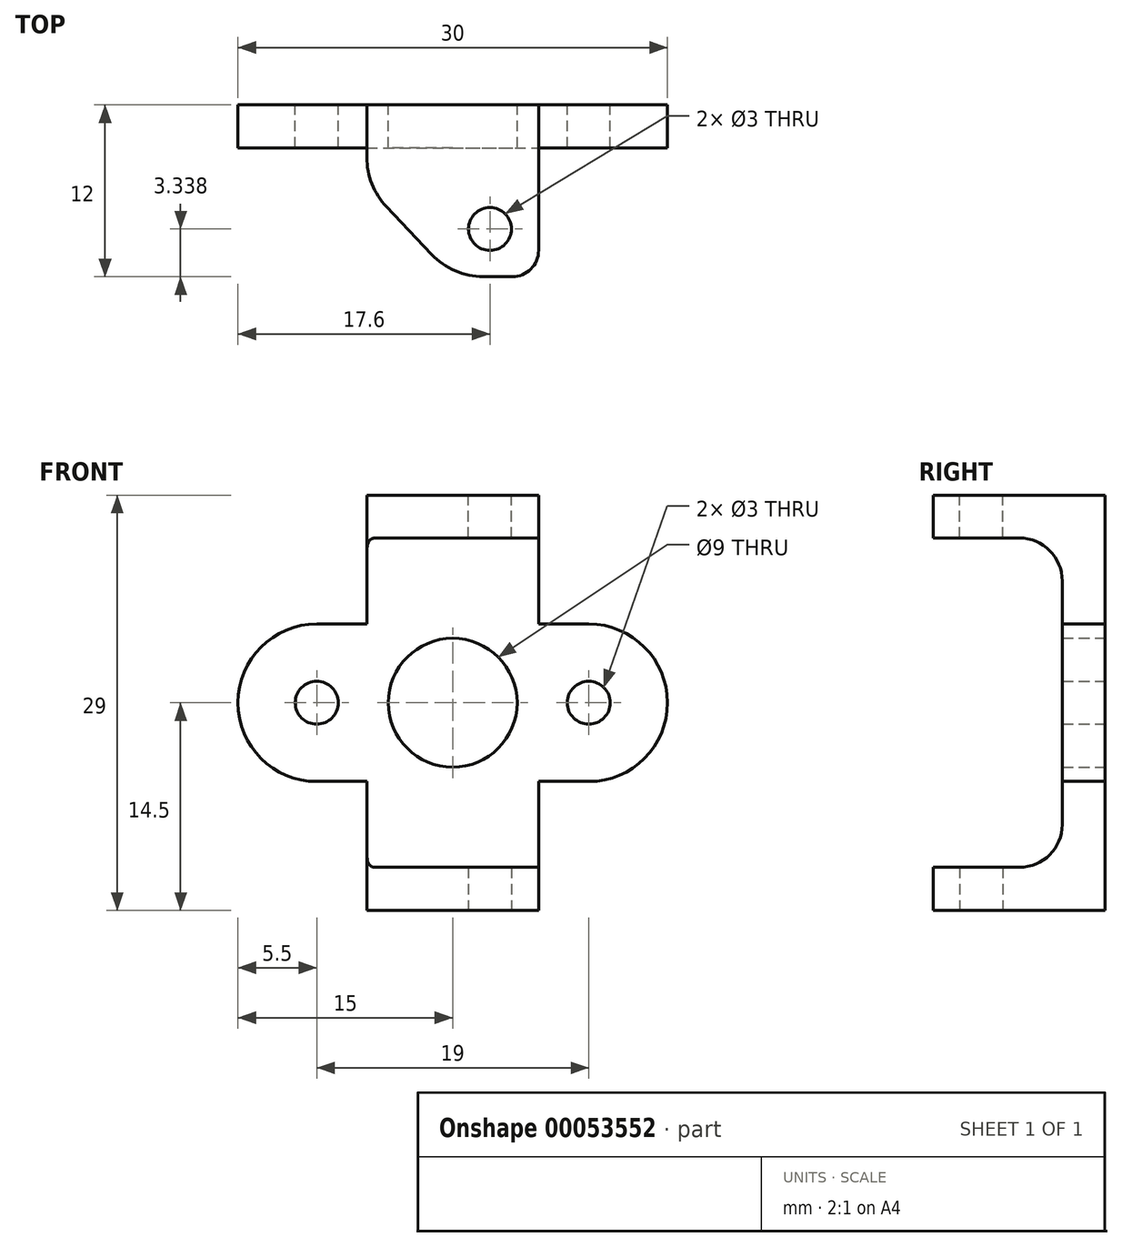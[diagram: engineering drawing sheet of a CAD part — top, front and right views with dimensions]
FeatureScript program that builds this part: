
annotation { "Feature Type Name" : "Feature", "Feature Type Description" : "" }
export const myFeature = defineFeature(function(context is Context, id is Id, definition is map)
    precondition{}
    {
        {
            var Q0;
            Q0=qCreatedBy(makeId("Front.planeOp"),FACE);
            var sketch = newSketch(context, id + "F0", { "sketchPlane" : qUnion([Q0])});
            skCircle(sketch, "E0", {"center": v(0, 0) * mm, "radius": 4.5 * mm});
            skCircle(sketch, "E1", {"center": v(9.5, 0) * mm, "radius": 1.5 * mm});
            skCircle(sketch, "E2.MirrorC", {"center": v(-9.5, 0) * mm, "radius": 1.5 * mm});
            skArc(sketch, "E3.0", {"start": v(9.5, -5.5) * mm, "mid": v(15, 0) * mm, "end": v(9.5, 5.5) * mm});
            skLineSegment(sketch, "E4", {"start": v(9.5, 7.45) * mm, "end": v(9.5, -7.59) * mm, "construction": true});
            skLineSegment(sketch, "E5", {"start": v(9.5, -5.5) * mm, "end": v(0, -5.5) * mm});
            skLineSegment(sketch, "E6.MirrorCS", {"start": v(9.5, 5.5) * mm, "end": v(0, 5.5) * mm});
            skArc(sketch, "E7.MirrorCS", {"start": v(-9.5, -5.5) * mm, "mid": v(-15, 0) * mm, "end": v(-9.5, 5.5) * mm});
            skLineSegment(sketch, "E8.MirrorCS", {"start": v(-9.5, 5.5) * mm, "end": v(0, 5.5) * mm});
            skLineSegment(sketch, "E9.MirrorCS", {"start": v(-9.5, -5.5) * mm, "end": v(0, -5.5) * mm});
            skSolve(sketch);
        }
        {
            var Q0;
            Q0 = qSketchRegion(id + "F0", true);
            extrude(context, id + "F1", {"entities" : qUnion([Q0]), "depth" : 3 * mm});
        }
        {
            var Q0;
            Q0=makeQuery(id+"F1.opExtrude","CAP_FACE",FACE,{"disambiguationData":[OSD([sQuery(id+"F0.wireOp",EDGE,"E0"),sQuery(id+"F0.wireOp",EDGE,"E1"),sQuery(id+"F0.wireOp",EDGE,"E2.MirrorC"),sQuery(id+"F0.wireOp",EDGE,"E3.0"),sQuery(id+"F0.wireOp",EDGE,"E5"),sQuery(id+"F0.wireOp",EDGE,"E6.MirrorCS"),sQuery(id+"F0.wireOp",EDGE,"E7.MirrorCS"),sQuery(id+"F0.wireOp",EDGE,"E8.MirrorCS"),sQuery(id+"F0.wireOp",EDGE,"E9.MirrorCS")])],"isStart":false});
            var sketch = newSketch(context, id + "F2", { "sketchPlane" : qUnion([Q0])});
            skLineSegment(sketch, "E10.rect.bottom", {"start": v(6, -14.5) * mm, "end": v(-6, -14.5) * mm});
            skLineSegment(sketch, "E10.rect.top", {"start": v(6, 14.5) * mm, "end": v(-6, 14.5) * mm});
            skLineSegment(sketch, "E10.rect.left", {"start": v(6, -14.5) * mm, "end": v(6, 14.5) * mm});
            skLineSegment(sketch, "E10.rect.right", {"start": v(-6, -14.5) * mm, "end": v(-6, 14.5) * mm});
            skPoint(sketch, "E10.rect.middle", {"position": v(0, 0) * mm});
            skSolve(sketch);
        }
        {
            var Q0;
            Q0 = qSketchRegion(id + "F2", true);
            extrude(context, id + "F3", {"entities" : qUnion([Q0]), "operationType" : NewBodyOperationType.ADD, "oppositeDirection" : true, "depth" : 3 * mm});
        }
        {
            var Q0;
            Q0=makeQuery(id+"F3.opExtrude","SWEPT_FACE",FACE,{"disambiguationData":[OSD([sQuery(id+"F2.wireOp",EDGE,"E10.rect.bottom")])]});
            var sketch = newSketch(context, id + "F4", { "sketchPlane" : qUnion([Q0])});
            skLineSegment(sketch, "E11.bottom", {"start": v(6, 0) * mm, "end": v(-6, 0) * mm});
            skLineSegment(sketch, "E11.top", {"start": v(4.15, 12) * mm, "end": v(2.15, 12) * mm});
            skLineSegment(sketch, "E11.left", {"start": v(6, 0) * mm, "end": v(6, 10.15) * mm});
            skLineSegment(sketch, "E11.right", {"start": v(-6, 0) * mm, "end": v(-6, 3.67) * mm});
            skPoint(sketch, "E12.visualSharp", {"position": v(6, 12) * mm});
            skArc(sketch, "E12.filletArc", {"start": v(6, 10.15) * mm, "mid": v(5.46, 11.46) * mm, "end": v(4.15, 12) * mm});
            skCircle(sketch, "E13", {"center": v(2.6, 8.66) * mm, "radius": 1.5 * mm});
            skLineSegment(sketch, "E14", {"start": v(-1.48, 10.44) * mm, "end": v(-4.63, 7.11) * mm});
            skPoint(sketch, "E15.orphan", {"position": v(-6, 12) * mm});
            skPoint(sketch, "E16.visualSharp", {"position": v(-6, 5.67) * mm});
            skArc(sketch, "E16.filletArc", {"start": v(-4.63, 7.11) * mm, "mid": v(-5.64, 5.53) * mm, "end": v(-6, 3.67) * mm});
            skPoint(sketch, "E17.visualSharp", {"position": v(0, 12) * mm});
            skArc(sketch, "E17.filletArc", {"start": v(2.15, 12) * mm, "mid": v(0.17, 11.6) * mm, "end": v(-1.48, 10.44) * mm});
            skSolve(sketch);
        }
        {
            var Q0;
            Q0 = qSketchRegion(id + "F4", true);
            extrude(context, id + "F5", {"entities" : qUnion([Q0]), "oppositeDirection" : true, "depth" : 3 * mm});
        }
        {
            var Q0;
            Q0=makeQuery(id+"F5.opExtrude","SWEPT_BODY",BODY,{"disambiguationData":[OSD([sQuery(id+"F4.wireOp",EDGE,"E11.bottom"),sQuery(id+"F4.wireOp",EDGE,"E11.top"),sQuery(id+"F4.wireOp",EDGE,"E11.left"),sQuery(id+"F4.wireOp",EDGE,"E11.right"),sQuery(id+"F4.wireOp",EDGE,"E12.filletArc"),sQuery(id+"F4.wireOp",EDGE,"E13"),sQuery(id+"F4.wireOp",EDGE,"E14"),sQuery(id+"F4.wireOp",EDGE,"E16.filletArc"),sQuery(id+"F4.wireOp",EDGE,"E17.filletArc")])]});
            var Q1;
            Q1=qCreatedBy(makeId("Top.planeOp"),FACE);
            mirror(context, id + "F6", {"operationType" : NewBodyOperationType.ADD, "entities" : qUnion([Q0]), "mirrorPlane" : qUnion([Q1])});
        }
        {
            var Q0;
            Q0=makeQuery(id+"F6.boolean.opBoolean","INTERSECT",EDGE,{"derivedFrom":[makeQuery(id+"F3.boolean.opBoolean","MERGE",FACE,{"derivedFrom":[makeQuery(id+"F1.opExtrude","CAP_FACE",FACE,{"disambiguationData":[OSD([sQuery(id+"F0.wireOp",EDGE,"E0"),sQuery(id+"F0.wireOp",EDGE,"E1"),sQuery(id+"F0.wireOp",EDGE,"E2.MirrorC"),sQuery(id+"F0.wireOp",EDGE,"E3.0"),sQuery(id+"F0.wireOp",EDGE,"E5"),sQuery(id+"F0.wireOp",EDGE,"E6.MirrorCS"),sQuery(id+"F0.wireOp",EDGE,"E7.MirrorCS"),sQuery(id+"F0.wireOp",EDGE,"E8.MirrorCS"),sQuery(id+"F0.wireOp",EDGE,"E9.MirrorCS")])],"isStart":false}),makeQuery(id+"F3.opExtrude","CAP_FACE",FACE,{"disambiguationData":[OSD([sQuery(id+"F2.wireOp",EDGE,"E10.rect.bottom"),sQuery(id+"F2.wireOp",EDGE,"E10.rect.top"),sQuery(id+"F2.wireOp",EDGE,"E10.rect.left"),sQuery(id+"F2.wireOp",EDGE,"E10.rect.right")])],"isStart":true})]}),makeQuery(id+"F6.opPattern","COPY",FACE,{"derivedFrom":makeQuery(id+"F5.opExtrude","CAP_FACE",FACE,{"disambiguationData":[OSD([sQuery(id+"F4.wireOp",EDGE,"E11.bottom"),sQuery(id+"F4.wireOp",EDGE,"E11.top"),sQuery(id+"F4.wireOp",EDGE,"E11.left"),sQuery(id+"F4.wireOp",EDGE,"E11.right"),sQuery(id+"F4.wireOp",EDGE,"E12.filletArc"),sQuery(id+"F4.wireOp",EDGE,"E13"),sQuery(id+"F4.wireOp",EDGE,"E14"),sQuery(id+"F4.wireOp",EDGE,"E16.filletArc"),sQuery(id+"F4.wireOp",EDGE,"E17.filletArc")])],"isStart":false}),"instanceName":"1"})]});
            var Q1;
            Q1=makeQuery(id+"F6.boolean.opBoolean","INTERSECT",EDGE,{"derivedFrom":[makeQuery(id+"F3.boolean.opBoolean","MERGE",FACE,{"derivedFrom":[makeQuery(id+"F1.opExtrude","CAP_FACE",FACE,{"disambiguationData":[OSD([sQuery(id+"F0.wireOp",EDGE,"E0"),sQuery(id+"F0.wireOp",EDGE,"E1"),sQuery(id+"F0.wireOp",EDGE,"E2.MirrorC"),sQuery(id+"F0.wireOp",EDGE,"E3.0"),sQuery(id+"F0.wireOp",EDGE,"E5"),sQuery(id+"F0.wireOp",EDGE,"E6.MirrorCS"),sQuery(id+"F0.wireOp",EDGE,"E7.MirrorCS"),sQuery(id+"F0.wireOp",EDGE,"E8.MirrorCS"),sQuery(id+"F0.wireOp",EDGE,"E9.MirrorCS")])],"isStart":false}),makeQuery(id+"F3.opExtrude","CAP_FACE",FACE,{"disambiguationData":[OSD([sQuery(id+"F2.wireOp",EDGE,"E10.rect.bottom"),sQuery(id+"F2.wireOp",EDGE,"E10.rect.top"),sQuery(id+"F2.wireOp",EDGE,"E10.rect.left"),sQuery(id+"F2.wireOp",EDGE,"E10.rect.right")])],"isStart":true})]}),makeQuery(id+"F5.opExtrude","CAP_FACE",FACE,{"disambiguationData":[OSD([sQuery(id+"F4.wireOp",EDGE,"E11.bottom"),sQuery(id+"F4.wireOp",EDGE,"E11.top"),sQuery(id+"F4.wireOp",EDGE,"E11.left"),sQuery(id+"F4.wireOp",EDGE,"E11.right"),sQuery(id+"F4.wireOp",EDGE,"E12.filletArc"),sQuery(id+"F4.wireOp",EDGE,"E13"),sQuery(id+"F4.wireOp",EDGE,"E14"),sQuery(id+"F4.wireOp",EDGE,"E16.filletArc"),sQuery(id+"F4.wireOp",EDGE,"E17.filletArc")])],"isStart":false})]});
            fillet(context, id + "F7", {"entities" : qUnion([Q0, Q1]), "radius" : 3 * mm, "tangentPropagation" : true, "allowEdgeOverflow" : false});
        }
        {
            var Q0;
            Q0=makeQuery(id+"F3.boolean.opBoolean","MERGE",FACE,{"derivedFrom":[makeQuery(id+"F1.opExtrude","CAP_FACE",FACE,{"disambiguationData":[OSD([sQuery(id+"F0.wireOp",EDGE,"E0"),sQuery(id+"F0.wireOp",EDGE,"E1"),sQuery(id+"F0.wireOp",EDGE,"E2.MirrorC"),sQuery(id+"F0.wireOp",EDGE,"E3.0"),sQuery(id+"F0.wireOp",EDGE,"E5"),sQuery(id+"F0.wireOp",EDGE,"E6.MirrorCS"),sQuery(id+"F0.wireOp",EDGE,"E7.MirrorCS"),sQuery(id+"F0.wireOp",EDGE,"E8.MirrorCS"),sQuery(id+"F0.wireOp",EDGE,"E9.MirrorCS")])],"isStart":true}),makeQuery(id+"F3.opExtrude","CAP_FACE",FACE,{"disambiguationData":[OSD([sQuery(id+"F2.wireOp",EDGE,"E10.rect.bottom"),sQuery(id+"F2.wireOp",EDGE,"E10.rect.top"),sQuery(id+"F2.wireOp",EDGE,"E10.rect.left"),sQuery(id+"F2.wireOp",EDGE,"E10.rect.right")])],"isStart":false})]});
            var sketch = newSketch(context, id + "F8", { "sketchPlane" : qUnion([Q0])});
            skCircle(sketch, "E18", {"center": v(0, 0) * mm, "radius": 4.5 * mm});
            skSolve(sketch);
        }
        {
            var Q0;
            Q0 = qSketchRegion(id + "F8", true);
            extrude(context, id + "F9", {"entities" : qUnion([Q0]), "operationType" : NewBodyOperationType.REMOVE, "endBound" : BoundingType.UP_TO_NEXT, "oppositeDirection" : true, "depth" : 25 * mm});
        }
    });
